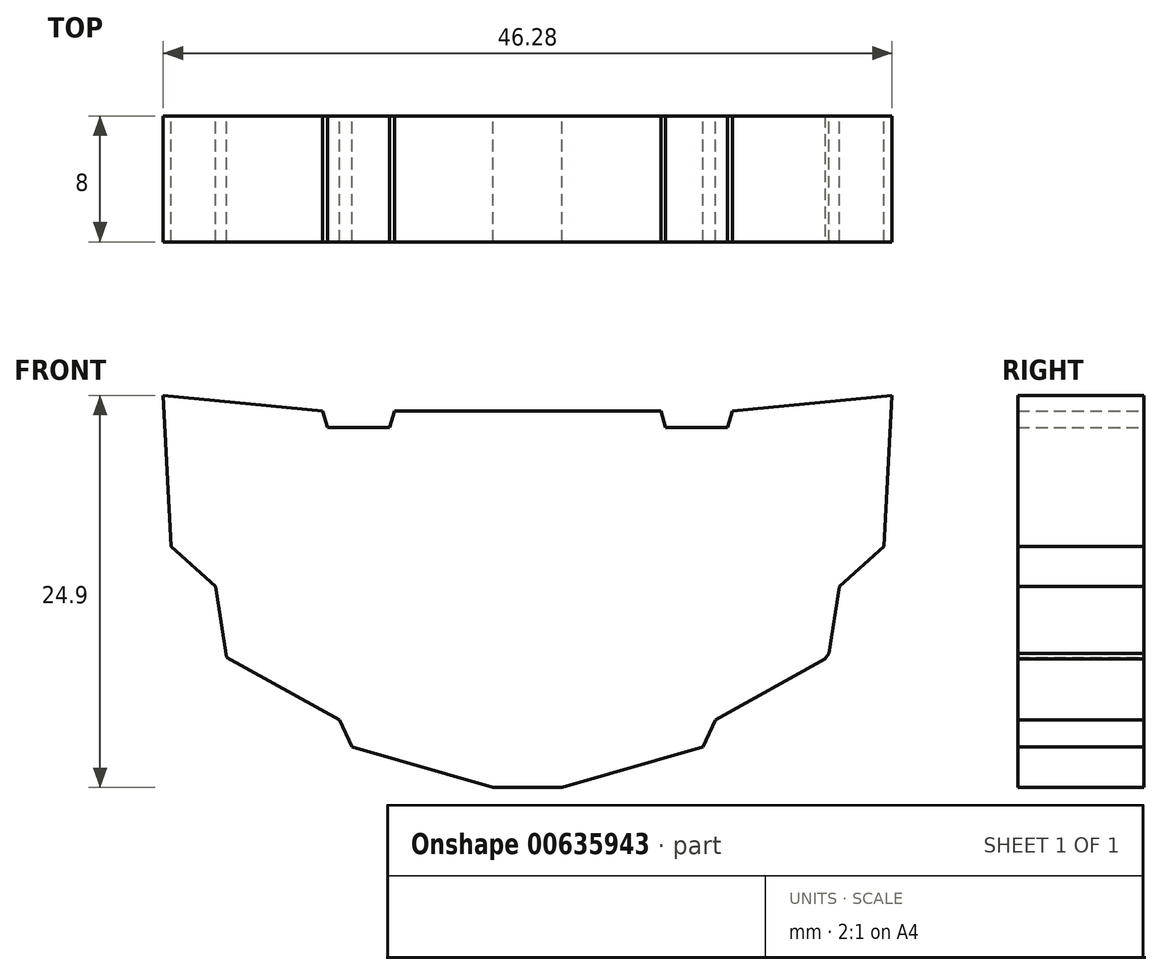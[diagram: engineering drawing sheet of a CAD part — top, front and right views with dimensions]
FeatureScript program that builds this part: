
annotation { "Feature Type Name" : "Feature", "Feature Type Description" : "" }
export const myFeature = defineFeature(function(context is Context, id is Id, definition is map)
    precondition{}
    {
        {
            var Q0;
            Q0=qCreatedBy(makeId("Front.planeOp"),FACE);
            var sketch = newSketch(context, id + "F0", { "sketchPlane" : qUnion([Q0])});
            skPoint(sketch, "E0.middle", {"position": v(0, 0) * mm});
            skLineSegment(sketch, "E1", {"start": v(-23.14, 12.14) * mm, "end": v(-13, 11.16) * mm});
            skLineSegment(sketch, "E2", {"start": v(-13, 11.16) * mm, "end": v(-12.69, 10.1) * mm});
            skLineSegment(sketch, "E3", {"start": v(-12.69, 10.1) * mm, "end": v(-8.75, 10.1) * mm});
            skLineSegment(sketch, "E4", {"start": v(-8.75, 10.1) * mm, "end": v(-8.46, 11.16) * mm});
            skLineSegment(sketch, "E5", {"start": v(-23.14, 12.14) * mm, "end": v(-22.63, 2.56) * mm});
            skLineSegment(sketch, "E6", {"start": v(-22.63, 2.56) * mm, "end": v(-19.8, 0) * mm});
            skLineSegment(sketch, "E7", {"start": v(-19.8, 0) * mm, "end": v(-19.11, -4.49) * mm});
            skLineSegment(sketch, "E8", {"start": v(-19.11, -4.49) * mm, "end": v(-11.95, -8.46) * mm});
            skLineSegment(sketch, "E9", {"start": v(-11.95, -8.46) * mm, "end": v(-11.14, -10.17) * mm});
            skLineSegment(sketch, "E10", {"start": v(-11.14, -10.17) * mm, "end": v(-2.18, -12.76) * mm});
            skLineSegment(sketch, "E11", {"start": v(-8.46, 11.16) * mm, "end": v(0, 11.16) * mm});
            skLineSegment(sketch, "E12", {"start": v(-2.18, -12.76) * mm, "end": v(0, -12.76) * mm});
            skLineSegment(sketch, "E13.MirrorCS", {"start": v(19.11, -4.49) * mm, "end": v(11.95, -8.46) * mm});
            skLineSegment(sketch, "E14.MirrorCS", {"start": v(8.46, 11.16) * mm, "end": v(0, 11.16) * mm});
            skLineSegment(sketch, "E15.MirrorCS", {"start": v(11.95, -8.46) * mm, "end": v(11.14, -10.17) * mm});
            skLineSegment(sketch, "E16.MirrorCS", {"start": v(12.69, 10.1) * mm, "end": v(8.75, 10.1) * mm});
            skLineSegment(sketch, "E17.MirrorCS", {"start": v(23.14, 12.14) * mm, "end": v(22.63, 2.56) * mm});
            skLineSegment(sketch, "E18.MirrorCS", {"start": v(2.18, -12.76) * mm, "end": v(0, -12.76) * mm});
            skLineSegment(sketch, "E19.MirrorCS", {"start": v(8.75, 10.1) * mm, "end": v(8.46, 11.16) * mm});
            skLineSegment(sketch, "E20.MirrorCS", {"start": v(11.14, -10.17) * mm, "end": v(2.18, -12.76) * mm});
            skLineSegment(sketch, "E21.MirrorCS", {"start": v(13, 11.16) * mm, "end": v(12.69, 10.1) * mm});
            skLineSegment(sketch, "E22.MirrorCS", {"start": v(23.14, 12.14) * mm, "end": v(13, 11.16) * mm});
            skLineSegment(sketch, "E23.MirrorCS", {"start": v(19.8, 0) * mm, "end": v(19.11, -4.49) * mm});
            skLineSegment(sketch, "E24.MirrorCS", {"start": v(22.63, 2.56) * mm, "end": v(19.8, 0) * mm});
            skLineSegment(sketch, "E25.bottom", {"start": v(24.25, 13.5) * mm, "end": v(-24.25, 13.5) * mm});
            skLineSegment(sketch, "E25.top", {"start": v(24.25, -13.5) * mm, "end": v(-24.25, -13.5) * mm});
            skLineSegment(sketch, "E25.left", {"start": v(24.25, 13.5) * mm, "end": v(24.25, -13.5) * mm});
            skLineSegment(sketch, "E25.right", {"start": v(-24.25, 13.5) * mm, "end": v(-24.25, -13.5) * mm});
            skSolve(sketch);
        }
        {
            var Q0;
            Q0=makeQuery(id+"F0.imprint","IMPRINT",FACE,{"disambiguationData":[TD([[makeQuery(id+"F0.imprint","IMPRINT",EDGE,{"derivedFrom":sQuery(id+"F0.wireOp",EDGE,"E1")}),-1.0]])]});
            extrude(context, id + "F1", {"entities" : qUnion([Q0]), "depth" : 8 * mm, "offsetDistance" : 25 * mm});
        }
        {
            var Q0;
            Q0=makeQuery(id+"F0.imprint","IMPRINT",FACE,{"disambiguationData":[TD([[makeQuery(id+"F0.imprint","IMPRINT",EDGE,{"derivedFrom":sQuery(id+"F0.wireOp",EDGE,"E1")}),-1.0]])]});
            extrude(context, id + "F2", {"entities" : qUnion([Q0]), "operationType" : NewBodyOperationType.ADD, "depth" : 8 * mm, "offsetDistance" : 25 * mm});
        }
        {
            var Q0;
            Q0=makeQuery(id+"F1.opExtrude","SWEPT_EDGE",EDGE,{"disambiguationData":[OSD([sQuery(id+"F0.wireOp",EDGE,"E13.MirrorCS"),sQuery(id+"F0.wireOp",EDGE,"E23.MirrorCS")])]});
            chamfer(context, id + "F3", {"entities" : qUnion([Q0]), "width" : 0.5 * mm, "tangentPropagation" : true});
        }
    });
